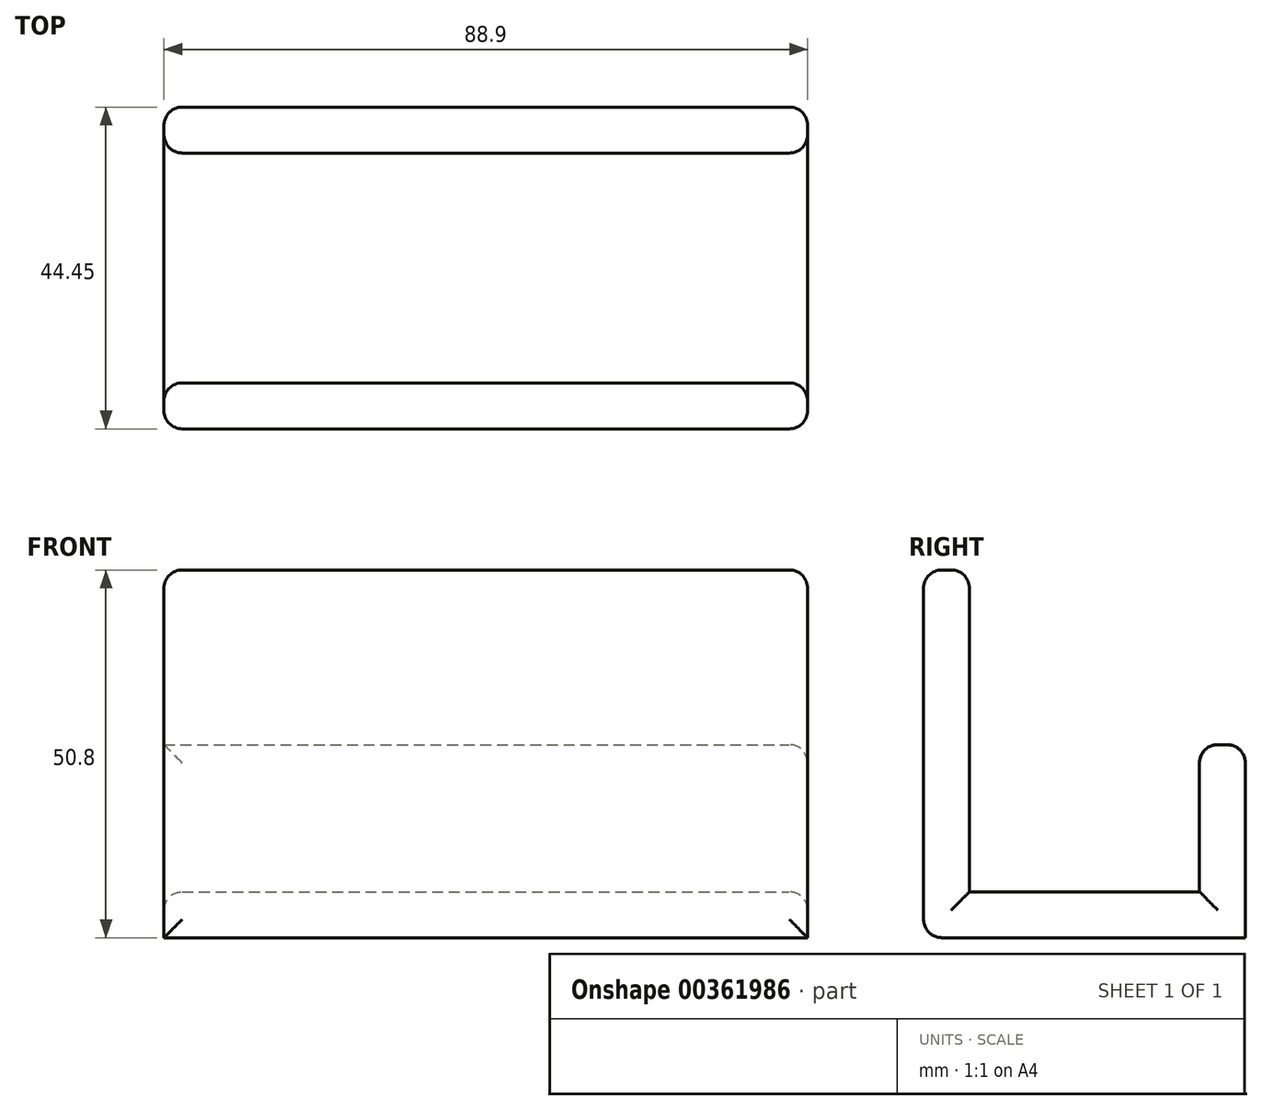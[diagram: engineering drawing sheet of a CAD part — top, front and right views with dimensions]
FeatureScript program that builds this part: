
annotation { "Feature Type Name" : "Feature", "Feature Type Description" : "" }
export const myFeature = defineFeature(function(context is Context, id is Id, definition is map)
    precondition{}
    {
        {
            var Q0;
            Q0=qCreatedBy(makeId("Right.planeOp"),FACE);
            var sketch = newSketch(context, id + "F0", { "sketchPlane" : qUnion([Q0])});
            skLineSegment(sketch, "E0.bottom", {"start": v(-44.67, 51.5) * mm, "end": v(-38.32, 51.5) * mm});
            skLineSegment(sketch, "E0.top", {"start": v(-44.67, 0.7) * mm, "end": v(-0.22, 0.7) * mm});
            skLineSegment(sketch, "E0.left", {"start": v(-44.67, 51.5) * mm, "end": v(-44.67, 0.7) * mm});
            skLineSegment(sketch, "E0.right", {"start": v(-0.22, 27.38) * mm, "end": v(-0.22, 0.7) * mm});
            skLineSegment(sketch, "E1", {"start": v(-38.32, 51.5) * mm, "end": v(-38.32, 7.06) * mm});
            skLineSegment(sketch, "E2", {"start": v(-38.32, 7.06) * mm, "end": v(-6.57, 7.06) * mm});
            skLineSegment(sketch, "E3", {"start": v(-6.57, 7.06) * mm, "end": v(-6.57, 27.38) * mm});
            skLineSegment(sketch, "E4", {"start": v(-6.57, 27.38) * mm, "end": v(-0.22, 27.38) * mm});
            skSolve(sketch);
        }
        {
            var Q0;
            Q0=makeQuery(id+"F0.imprint","IMPRINT",FACE,{"disambiguationData":[TD([[makeQuery(id+"F0.imprint","IMPRINT",EDGE,{"derivedFrom":sQuery(id+"F0.wireOp",EDGE,"E0.bottom")}),-1.0]])]});
            extrude(context, id + "F1", {"entities" : qUnion([Q0]), "oppositeDirection" : true, "depth" : 88.9 * mm});
        }
        {
            var Q0;
            Q0=makeQuery(id+"F1.opExtrude","SWEPT_EDGE",EDGE,{"disambiguationData":[OSD([sQuery(id+"F0.wireOp",EDGE,"E0.right"),sQuery(id+"F0.wireOp",EDGE,"E4")])]});
            var Q1;
            Q1=makeQuery(id+"F1.opExtrude","SWEPT_EDGE",EDGE,{"disambiguationData":[OSD([sQuery(id+"F0.wireOp",EDGE,"E3"),sQuery(id+"F0.wireOp",EDGE,"E4")])]});
            var Q2;
            Q2=makeQuery(id+"F1.opExtrude","SWEPT_EDGE",EDGE,{"disambiguationData":[OSD([sQuery(id+"F0.wireOp",EDGE,"E0.bottom"),sQuery(id+"F0.wireOp",EDGE,"E1")])]});
            var Q3;
            Q3=makeQuery(id+"F1.opExtrude","CAP_EDGE",EDGE,{"disambiguationData":[OSD([sQuery(id+"F0.wireOp",EDGE,"E3")])],"isStart":false});
            var Q4;
            Q4=makeQuery(id+"F1.opExtrude","CAP_EDGE",EDGE,{"disambiguationData":[OSD([sQuery(id+"F0.wireOp",EDGE,"E2")])],"isStart":false});
            var Q5;
            Q5=makeQuery(id+"F1.opExtrude","CAP_EDGE",EDGE,{"disambiguationData":[OSD([sQuery(id+"F0.wireOp",EDGE,"E1")])],"isStart":false});
            var Q6;
            Q6=makeQuery(id+"F1.opExtrude","CAP_EDGE",EDGE,{"disambiguationData":[OSD([sQuery(id+"F0.wireOp",EDGE,"E0.left")])],"isStart":false});
            var Q7;
            Q7=makeQuery(id+"F1.opExtrude","CAP_EDGE",EDGE,{"disambiguationData":[OSD([sQuery(id+"F0.wireOp",EDGE,"E0.bottom")])],"isStart":false});
            var Q8;
            Q8=makeQuery(id+"F1.opExtrude","CAP_EDGE",EDGE,{"disambiguationData":[OSD([sQuery(id+"F0.wireOp",EDGE,"E0.right")])],"isStart":false});
            var Q9;
            Q9=makeQuery(id+"F1.opExtrude","CAP_EDGE",EDGE,{"disambiguationData":[OSD([sQuery(id+"F0.wireOp",EDGE,"E0.bottom")])],"isStart":true});
            var Q10;
            Q10=makeQuery(id+"F1.opExtrude","CAP_EDGE",EDGE,{"disambiguationData":[OSD([sQuery(id+"F0.wireOp",EDGE,"E1")])],"isStart":true});
            var Q11;
            Q11=makeQuery(id+"F1.opExtrude","CAP_EDGE",EDGE,{"disambiguationData":[OSD([sQuery(id+"F0.wireOp",EDGE,"E0.left")])],"isStart":true});
            var Q12;
            Q12=makeQuery(id+"F1.opExtrude","CAP_EDGE",EDGE,{"disambiguationData":[OSD([sQuery(id+"F0.wireOp",EDGE,"E2")])],"isStart":true});
            var Q13;
            Q13=makeQuery(id+"F1.opExtrude","CAP_EDGE",EDGE,{"disambiguationData":[OSD([sQuery(id+"F0.wireOp",EDGE,"E3")])],"isStart":true});
            var Q14;
            Q14=makeQuery(id+"F1.opExtrude","CAP_EDGE",EDGE,{"disambiguationData":[OSD([sQuery(id+"F0.wireOp",EDGE,"E4")])],"isStart":true});
            var Q15;
            Q15=makeQuery(id+"F1.opExtrude","CAP_EDGE",EDGE,{"disambiguationData":[OSD([sQuery(id+"F0.wireOp",EDGE,"E0.right")])],"isStart":true});
            var Q16;
            Q16=makeQuery(id+"F1.opExtrude","SWEPT_EDGE",EDGE,{"disambiguationData":[OSD([sQuery(id+"F0.wireOp",EDGE,"E0.bottom"),sQuery(id+"F0.wireOp",EDGE,"E0.left")])]});
            var Q17;
            Q17=makeQuery(id+"F1.opExtrude","SWEPT_FACE",FACE,{"disambiguationData":[OSD([sQuery(id+"F0.wireOp",EDGE,"E0.left")])]});
            fillet(context, id + "F2", {"entities" : qUnion([Q0, Q1, Q2, Q3, Q4, Q5, Q6, Q7, Q8, Q9, Q10, Q11, Q12, Q13, Q14, Q15, Q16, Q17]), "radius" : 2.54 * mm, "tangentPropagation" : true, "allowEdgeOverflow" : false});
        }
    });
